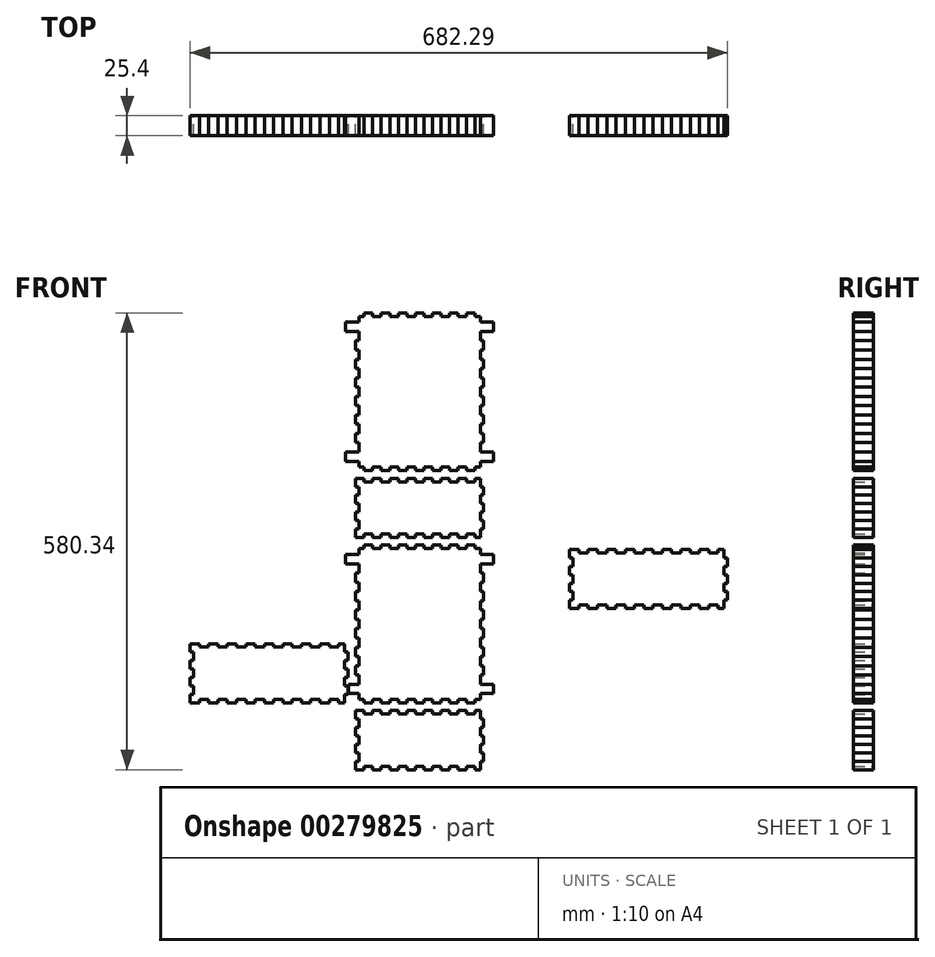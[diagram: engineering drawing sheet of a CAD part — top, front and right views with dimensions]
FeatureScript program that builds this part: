
annotation { "Feature Type Name" : "Feature", "Feature Type Description" : "" }
export const myFeature = defineFeature(function(context is Context, id is Id, definition is map)
    precondition{}
    {
        {
            var Q0;
            Q0=qCreatedBy(makeId("Front.planeOp"),FACE);
            var sketch = newSketch(context, id + "F0", { "sketchPlane" : qUnion([Q0])});
            skLineSegment(sketch, "E0", {"start": v(-81.37, -290.17) * mm, "end": v(-70.52, -290.17) * mm});
            skLineSegment(sketch, "E1", {"start": v(-70.52, -285.8) * mm, "end": v(-70.52, -290.17) * mm});
            skLineSegment(sketch, "E2", {"start": v(-70.52, -285.8) * mm, "end": v(-59.67, -285.8) * mm});
            skLineSegment(sketch, "E3", {"start": v(-59.67, -285.8) * mm, "end": v(-59.67, -290.17) * mm});
            skLineSegment(sketch, "E4", {"start": v(-59.67, -290.17) * mm, "end": v(-48.82, -290.17) * mm});
            skLineSegment(sketch, "E5", {"start": v(-48.82, -285.8) * mm, "end": v(-48.82, -290.17) * mm});
            skLineSegment(sketch, "E6", {"start": v(-48.82, -285.8) * mm, "end": v(-37.97, -285.8) * mm});
            skLineSegment(sketch, "E7", {"start": v(-37.97, -285.8) * mm, "end": v(-37.97, -290.17) * mm});
            skLineSegment(sketch, "E8", {"start": v(-37.97, -290.17) * mm, "end": v(-27.12, -290.17) * mm});
            skLineSegment(sketch, "E9", {"start": v(-27.12, -285.8) * mm, "end": v(-27.12, -290.17) * mm});
            skLineSegment(sketch, "E10", {"start": v(-27.12, -285.8) * mm, "end": v(-16.27, -285.8) * mm});
            skLineSegment(sketch, "E11", {"start": v(-16.27, -285.8) * mm, "end": v(-16.27, -290.17) * mm});
            skLineSegment(sketch, "E12", {"start": v(-16.27, -290.17) * mm, "end": v(-5.42, -290.17) * mm});
            skLineSegment(sketch, "E13", {"start": v(-5.42, -285.8) * mm, "end": v(-5.42, -290.17) * mm});
            skLineSegment(sketch, "E14", {"start": v(-5.42, -285.8) * mm, "end": v(5.42, -285.8) * mm});
            skLineSegment(sketch, "E15", {"start": v(5.42, -285.8) * mm, "end": v(5.42, -290.17) * mm});
            skLineSegment(sketch, "E16", {"start": v(5.42, -290.17) * mm, "end": v(16.27, -290.17) * mm});
            skLineSegment(sketch, "E17", {"start": v(16.27, -285.8) * mm, "end": v(16.27, -290.17) * mm});
            skLineSegment(sketch, "E18", {"start": v(16.27, -285.8) * mm, "end": v(27.12, -285.8) * mm});
            skLineSegment(sketch, "E19", {"start": v(27.12, -285.8) * mm, "end": v(27.12, -290.17) * mm});
            skLineSegment(sketch, "E20", {"start": v(27.12, -290.17) * mm, "end": v(37.97, -290.17) * mm});
            skLineSegment(sketch, "E21", {"start": v(37.97, -285.8) * mm, "end": v(37.97, -290.17) * mm});
            skLineSegment(sketch, "E22", {"start": v(37.97, -285.8) * mm, "end": v(48.82, -285.8) * mm});
            skLineSegment(sketch, "E23", {"start": v(48.82, -285.8) * mm, "end": v(48.82, -290.17) * mm});
            skLineSegment(sketch, "E24", {"start": v(48.82, -290.17) * mm, "end": v(59.67, -290.17) * mm});
            skLineSegment(sketch, "E25", {"start": v(59.67, -285.8) * mm, "end": v(59.67, -290.17) * mm});
            skLineSegment(sketch, "E26", {"start": v(59.67, -285.8) * mm, "end": v(70.51, -285.8) * mm});
            skLineSegment(sketch, "E27", {"start": v(70.51, -285.8) * mm, "end": v(70.51, -290.17) * mm});
            skLineSegment(sketch, "E28", {"start": v(70.51, -290.17) * mm, "end": v(76.98, -290.17) * mm});
            skLineSegment(sketch, "E29", {"start": v(-81.37, -215.07) * mm, "end": v(-70.52, -215.07) * mm});
            skLineSegment(sketch, "E30", {"start": v(-70.52, -215.07) * mm, "end": v(-70.52, -219.45) * mm});
            skLineSegment(sketch, "E31", {"start": v(-70.52, -219.45) * mm, "end": v(-59.67, -219.45) * mm});
            skLineSegment(sketch, "E32", {"start": v(-59.67, -215.07) * mm, "end": v(-59.67, -219.45) * mm});
            skLineSegment(sketch, "E33", {"start": v(-59.67, -215.07) * mm, "end": v(-48.82, -215.07) * mm});
            skLineSegment(sketch, "E34", {"start": v(-48.82, -215.07) * mm, "end": v(-48.82, -219.45) * mm});
            skLineSegment(sketch, "E35", {"start": v(-48.82, -219.45) * mm, "end": v(-37.97, -219.45) * mm});
            skLineSegment(sketch, "E36", {"start": v(-37.97, -215.07) * mm, "end": v(-37.97, -219.45) * mm});
            skLineSegment(sketch, "E37", {"start": v(-37.97, -215.07) * mm, "end": v(-27.12, -215.07) * mm});
            skLineSegment(sketch, "E38", {"start": v(-27.12, -215.07) * mm, "end": v(-27.12, -219.45) * mm});
            skLineSegment(sketch, "E39", {"start": v(-27.12, -219.45) * mm, "end": v(-16.27, -219.45) * mm});
            skLineSegment(sketch, "E40", {"start": v(-16.27, -215.07) * mm, "end": v(-16.27, -219.45) * mm});
            skLineSegment(sketch, "E41", {"start": v(-16.27, -215.07) * mm, "end": v(-5.42, -215.07) * mm});
            skLineSegment(sketch, "E42", {"start": v(-5.42, -215.07) * mm, "end": v(-5.42, -219.45) * mm});
            skLineSegment(sketch, "E43", {"start": v(-5.42, -219.45) * mm, "end": v(5.42, -219.45) * mm});
            skLineSegment(sketch, "E44", {"start": v(5.42, -215.07) * mm, "end": v(5.42, -219.45) * mm});
            skLineSegment(sketch, "E45", {"start": v(5.42, -215.07) * mm, "end": v(16.27, -215.07) * mm});
            skLineSegment(sketch, "E46", {"start": v(16.27, -215.07) * mm, "end": v(16.27, -219.45) * mm});
            skLineSegment(sketch, "E47", {"start": v(16.27, -219.45) * mm, "end": v(27.12, -219.45) * mm});
            skLineSegment(sketch, "E48", {"start": v(27.12, -215.07) * mm, "end": v(27.12, -219.45) * mm});
            skLineSegment(sketch, "E49", {"start": v(27.12, -215.07) * mm, "end": v(37.97, -215.07) * mm});
            skLineSegment(sketch, "E50", {"start": v(37.97, -215.07) * mm, "end": v(37.97, -219.45) * mm});
            skLineSegment(sketch, "E51", {"start": v(37.97, -219.45) * mm, "end": v(48.82, -219.45) * mm});
            skLineSegment(sketch, "E52", {"start": v(48.82, -215.07) * mm, "end": v(48.82, -219.45) * mm});
            skLineSegment(sketch, "E53", {"start": v(48.82, -215.07) * mm, "end": v(59.67, -215.07) * mm});
            skLineSegment(sketch, "E54", {"start": v(59.67, -215.07) * mm, "end": v(59.67, -219.45) * mm});
            skLineSegment(sketch, "E55", {"start": v(59.67, -219.45) * mm, "end": v(70.51, -219.45) * mm});
            skLineSegment(sketch, "E56", {"start": v(70.51, -215.07) * mm, "end": v(70.51, -219.45) * mm});
            skLineSegment(sketch, "E57", {"start": v(70.51, -215.07) * mm, "end": v(76.98, -215.07) * mm});
            skLineSegment(sketch, "E58", {"start": v(-81.37, -290.17) * mm, "end": v(-81.37, -279.44) * mm});
            skLineSegment(sketch, "E59", {"start": v(-76.98, -279.44) * mm, "end": v(-81.37, -279.44) * mm});
            skLineSegment(sketch, "E60", {"start": v(-76.98, -279.44) * mm, "end": v(-76.98, -268.71) * mm});
            skLineSegment(sketch, "E61", {"start": v(-76.98, -268.71) * mm, "end": v(-81.37, -268.71) * mm});
            skLineSegment(sketch, "E62", {"start": v(-81.37, -268.71) * mm, "end": v(-81.37, -257.99) * mm});
            skLineSegment(sketch, "E63", {"start": v(-76.98, -257.99) * mm, "end": v(-81.37, -257.99) * mm});
            skLineSegment(sketch, "E64", {"start": v(-76.98, -257.99) * mm, "end": v(-76.98, -247.26) * mm});
            skLineSegment(sketch, "E65", {"start": v(-76.98, -247.26) * mm, "end": v(-81.37, -247.26) * mm});
            skLineSegment(sketch, "E66", {"start": v(-81.37, -247.26) * mm, "end": v(-81.37, -236.53) * mm});
            skLineSegment(sketch, "E67", {"start": v(-76.98, -236.53) * mm, "end": v(-81.37, -236.53) * mm});
            skLineSegment(sketch, "E68", {"start": v(-76.98, -236.53) * mm, "end": v(-76.98, -225.8) * mm});
            skLineSegment(sketch, "E69", {"start": v(-76.98, -225.8) * mm, "end": v(-81.37, -225.8) * mm});
            skLineSegment(sketch, "E70", {"start": v(-81.37, -225.8) * mm, "end": v(-81.37, -215.07) * mm});
            skLineSegment(sketch, "E71", {"start": v(76.98, -290.17) * mm, "end": v(76.98, -279.44) * mm});
            skLineSegment(sketch, "E72", {"start": v(81.36, -279.44) * mm, "end": v(76.98, -279.44) * mm});
            skLineSegment(sketch, "E73", {"start": v(81.36, -279.44) * mm, "end": v(81.36, -268.71) * mm});
            skLineSegment(sketch, "E74", {"start": v(81.36, -268.71) * mm, "end": v(76.98, -268.71) * mm});
            skLineSegment(sketch, "E75", {"start": v(76.98, -268.71) * mm, "end": v(76.98, -257.99) * mm});
            skLineSegment(sketch, "E76", {"start": v(81.36, -257.99) * mm, "end": v(76.98, -257.99) * mm});
            skLineSegment(sketch, "E77", {"start": v(81.36, -257.99) * mm, "end": v(81.36, -247.26) * mm});
            skLineSegment(sketch, "E78", {"start": v(81.36, -247.26) * mm, "end": v(76.98, -247.26) * mm});
            skLineSegment(sketch, "E79", {"start": v(76.98, -247.26) * mm, "end": v(76.98, -236.53) * mm});
            skLineSegment(sketch, "E80", {"start": v(81.36, -236.53) * mm, "end": v(76.98, -236.53) * mm});
            skLineSegment(sketch, "E81", {"start": v(81.36, -236.53) * mm, "end": v(81.36, -225.8) * mm});
            skLineSegment(sketch, "E82", {"start": v(81.36, -225.8) * mm, "end": v(76.98, -225.8) * mm});
            skLineSegment(sketch, "E83", {"start": v(76.98, -225.8) * mm, "end": v(76.98, -215.07) * mm});
            skLineSegment(sketch, "E84", {"start": v(-291.5, -205.21) * mm, "end": v(-279.72, -205.21) * mm});
            skLineSegment(sketch, "E85", {"start": v(-279.72, -200.83) * mm, "end": v(-279.72, -205.21) * mm});
            skLineSegment(sketch, "E86", {"start": v(-279.72, -200.83) * mm, "end": v(-267.94, -200.83) * mm});
            skLineSegment(sketch, "E87", {"start": v(-267.94, -200.83) * mm, "end": v(-267.94, -205.21) * mm});
            skLineSegment(sketch, "E88", {"start": v(-267.94, -205.21) * mm, "end": v(-256.16, -205.21) * mm});
            skLineSegment(sketch, "E89", {"start": v(-256.16, -200.83) * mm, "end": v(-256.16, -205.21) * mm});
            skLineSegment(sketch, "E90", {"start": v(-256.16, -200.83) * mm, "end": v(-244.38, -200.83) * mm});
            skLineSegment(sketch, "E91", {"start": v(-244.38, -200.83) * mm, "end": v(-244.38, -205.21) * mm});
            skLineSegment(sketch, "E92", {"start": v(-244.38, -205.21) * mm, "end": v(-232.6, -205.21) * mm});
            skLineSegment(sketch, "E93", {"start": v(-232.6, -200.83) * mm, "end": v(-232.6, -205.21) * mm});
            skLineSegment(sketch, "E94", {"start": v(-232.6, -200.83) * mm, "end": v(-220.81, -200.83) * mm});
            skLineSegment(sketch, "E95", {"start": v(-220.81, -200.83) * mm, "end": v(-220.81, -205.21) * mm});
            skLineSegment(sketch, "E96", {"start": v(-220.81, -205.21) * mm, "end": v(-209.03, -205.21) * mm});
            skLineSegment(sketch, "E97", {"start": v(-209.03, -200.83) * mm, "end": v(-209.03, -205.21) * mm});
            skLineSegment(sketch, "E98", {"start": v(-209.03, -200.83) * mm, "end": v(-197.25, -200.83) * mm});
            skLineSegment(sketch, "E99", {"start": v(-197.25, -200.83) * mm, "end": v(-197.25, -205.21) * mm});
            skLineSegment(sketch, "E100", {"start": v(-197.25, -205.21) * mm, "end": v(-185.47, -205.21) * mm});
            skLineSegment(sketch, "E101", {"start": v(-185.47, -200.83) * mm, "end": v(-185.47, -205.21) * mm});
            skLineSegment(sketch, "E102", {"start": v(-185.47, -200.83) * mm, "end": v(-173.69, -200.83) * mm});
            skLineSegment(sketch, "E103", {"start": v(-173.69, -200.83) * mm, "end": v(-173.69, -205.21) * mm});
            skLineSegment(sketch, "E104", {"start": v(-173.69, -205.21) * mm, "end": v(-161.9, -205.21) * mm});
            skLineSegment(sketch, "E105", {"start": v(-161.9, -200.83) * mm, "end": v(-161.9, -205.21) * mm});
            skLineSegment(sketch, "E106", {"start": v(-161.9, -200.83) * mm, "end": v(-150.13, -200.83) * mm});
            skLineSegment(sketch, "E107", {"start": v(-150.13, -200.83) * mm, "end": v(-150.13, -205.21) * mm});
            skLineSegment(sketch, "E108", {"start": v(-150.13, -205.21) * mm, "end": v(-138.35, -205.21) * mm});
            skLineSegment(sketch, "E109", {"start": v(-138.35, -200.83) * mm, "end": v(-138.35, -205.21) * mm});
            skLineSegment(sketch, "E110", {"start": v(-138.35, -200.83) * mm, "end": v(-126.56, -200.83) * mm});
            skLineSegment(sketch, "E111", {"start": v(-126.56, -200.83) * mm, "end": v(-126.56, -205.21) * mm});
            skLineSegment(sketch, "E112", {"start": v(-126.56, -205.21) * mm, "end": v(-114.78, -205.21) * mm});
            skLineSegment(sketch, "E113", {"start": v(-114.78, -200.83) * mm, "end": v(-114.78, -205.21) * mm});
            skLineSegment(sketch, "E114", {"start": v(-114.78, -200.83) * mm, "end": v(-103, -200.83) * mm});
            skLineSegment(sketch, "E115", {"start": v(-103, -200.83) * mm, "end": v(-103, -205.21) * mm});
            skLineSegment(sketch, "E116", {"start": v(-103, -205.21) * mm, "end": v(-95.6, -205.21) * mm});
            skLineSegment(sketch, "E117", {"start": v(-291.5, -130.1) * mm, "end": v(-279.72, -130.1) * mm});
            skLineSegment(sketch, "E118", {"start": v(-279.72, -130.1) * mm, "end": v(-279.72, -134.49) * mm});
            skLineSegment(sketch, "E119", {"start": v(-279.72, -134.49) * mm, "end": v(-267.94, -134.49) * mm});
            skLineSegment(sketch, "E120", {"start": v(-267.94, -130.1) * mm, "end": v(-267.94, -134.49) * mm});
            skLineSegment(sketch, "E121", {"start": v(-267.94, -130.1) * mm, "end": v(-256.16, -130.1) * mm});
            skLineSegment(sketch, "E122", {"start": v(-256.16, -130.1) * mm, "end": v(-256.16, -134.49) * mm});
            skLineSegment(sketch, "E123", {"start": v(-256.16, -134.49) * mm, "end": v(-244.38, -134.49) * mm});
            skLineSegment(sketch, "E124", {"start": v(-244.38, -130.1) * mm, "end": v(-244.38, -134.49) * mm});
            skLineSegment(sketch, "E125", {"start": v(-244.38, -130.1) * mm, "end": v(-232.6, -130.1) * mm});
            skLineSegment(sketch, "E126", {"start": v(-232.6, -130.1) * mm, "end": v(-232.6, -134.49) * mm});
            skLineSegment(sketch, "E127", {"start": v(-232.6, -134.49) * mm, "end": v(-220.81, -134.49) * mm});
            skLineSegment(sketch, "E128", {"start": v(-220.81, -130.1) * mm, "end": v(-220.81, -134.49) * mm});
            skLineSegment(sketch, "E129", {"start": v(-220.81, -130.1) * mm, "end": v(-209.03, -130.1) * mm});
            skLineSegment(sketch, "E130", {"start": v(-209.03, -130.1) * mm, "end": v(-209.03, -134.49) * mm});
            skLineSegment(sketch, "E131", {"start": v(-209.03, -134.49) * mm, "end": v(-197.25, -134.49) * mm});
            skLineSegment(sketch, "E132", {"start": v(-197.25, -130.1) * mm, "end": v(-197.25, -134.49) * mm});
            skLineSegment(sketch, "E133", {"start": v(-197.25, -130.1) * mm, "end": v(-185.47, -130.1) * mm});
            skLineSegment(sketch, "E134", {"start": v(-185.47, -130.1) * mm, "end": v(-185.47, -134.49) * mm});
            skLineSegment(sketch, "E135", {"start": v(-185.47, -134.49) * mm, "end": v(-173.69, -134.49) * mm});
            skLineSegment(sketch, "E136", {"start": v(-173.69, -130.1) * mm, "end": v(-173.69, -134.49) * mm});
            skLineSegment(sketch, "E137", {"start": v(-173.69, -130.1) * mm, "end": v(-161.9, -130.1) * mm});
            skLineSegment(sketch, "E138", {"start": v(-161.9, -130.1) * mm, "end": v(-161.9, -134.49) * mm});
            skLineSegment(sketch, "E139", {"start": v(-161.9, -134.49) * mm, "end": v(-150.13, -134.49) * mm});
            skLineSegment(sketch, "E140", {"start": v(-150.13, -130.1) * mm, "end": v(-150.13, -134.49) * mm});
            skLineSegment(sketch, "E141", {"start": v(-150.13, -130.1) * mm, "end": v(-138.35, -130.1) * mm});
            skLineSegment(sketch, "E142", {"start": v(-138.35, -130.1) * mm, "end": v(-138.35, -134.49) * mm});
            skLineSegment(sketch, "E143", {"start": v(-138.35, -134.49) * mm, "end": v(-126.56, -134.49) * mm});
            skLineSegment(sketch, "E144", {"start": v(-126.56, -130.1) * mm, "end": v(-126.56, -134.49) * mm});
            skLineSegment(sketch, "E145", {"start": v(-126.56, -130.1) * mm, "end": v(-114.78, -130.1) * mm});
            skLineSegment(sketch, "E146", {"start": v(-114.78, -130.1) * mm, "end": v(-114.78, -134.49) * mm});
            skLineSegment(sketch, "E147", {"start": v(-114.78, -134.49) * mm, "end": v(-103, -134.49) * mm});
            skLineSegment(sketch, "E148", {"start": v(-103, -130.1) * mm, "end": v(-103, -134.49) * mm});
            skLineSegment(sketch, "E149", {"start": v(-103, -130.1) * mm, "end": v(-95.6, -130.1) * mm});
            skLineSegment(sketch, "E150", {"start": v(-291.5, -205.21) * mm, "end": v(-291.5, -194.48) * mm});
            skLineSegment(sketch, "E151", {"start": v(-287.12, -194.48) * mm, "end": v(-291.5, -194.48) * mm});
            skLineSegment(sketch, "E152", {"start": v(-287.12, -194.48) * mm, "end": v(-287.12, -183.75) * mm});
            skLineSegment(sketch, "E153", {"start": v(-287.12, -183.75) * mm, "end": v(-291.5, -183.75) * mm});
            skLineSegment(sketch, "E154", {"start": v(-291.5, -183.75) * mm, "end": v(-291.5, -173.02) * mm});
            skLineSegment(sketch, "E155", {"start": v(-287.12, -173.02) * mm, "end": v(-291.5, -173.02) * mm});
            skLineSegment(sketch, "E156", {"start": v(-287.12, -173.02) * mm, "end": v(-287.12, -162.3) * mm});
            skLineSegment(sketch, "E157", {"start": v(-287.12, -162.3) * mm, "end": v(-291.5, -162.3) * mm});
            skLineSegment(sketch, "E158", {"start": v(-291.5, -162.3) * mm, "end": v(-291.5, -151.56) * mm});
            skLineSegment(sketch, "E159", {"start": v(-287.12, -151.56) * mm, "end": v(-291.5, -151.56) * mm});
            skLineSegment(sketch, "E160", {"start": v(-287.12, -151.56) * mm, "end": v(-287.12, -140.84) * mm});
            skLineSegment(sketch, "E161", {"start": v(-287.12, -140.84) * mm, "end": v(-291.5, -140.84) * mm});
            skLineSegment(sketch, "E162", {"start": v(-291.5, -140.84) * mm, "end": v(-291.5, -130.1) * mm});
            skLineSegment(sketch, "E163", {"start": v(-95.6, -205.21) * mm, "end": v(-95.6, -194.48) * mm});
            skLineSegment(sketch, "E164", {"start": v(-91.22, -194.48) * mm, "end": v(-95.6, -194.48) * mm});
            skLineSegment(sketch, "E165", {"start": v(-91.22, -194.48) * mm, "end": v(-91.22, -183.75) * mm});
            skLineSegment(sketch, "E166", {"start": v(-91.22, -183.75) * mm, "end": v(-95.6, -183.75) * mm});
            skLineSegment(sketch, "E167", {"start": v(-95.6, -183.75) * mm, "end": v(-95.6, -173.02) * mm});
            skLineSegment(sketch, "E168", {"start": v(-91.22, -173.02) * mm, "end": v(-95.6, -173.02) * mm});
            skLineSegment(sketch, "E169", {"start": v(-91.22, -173.02) * mm, "end": v(-91.22, -162.3) * mm});
            skLineSegment(sketch, "E170", {"start": v(-91.22, -162.3) * mm, "end": v(-95.6, -162.3) * mm});
            skLineSegment(sketch, "E171", {"start": v(-95.6, -162.3) * mm, "end": v(-95.6, -151.56) * mm});
            skLineSegment(sketch, "E172", {"start": v(-91.22, -151.56) * mm, "end": v(-95.6, -151.56) * mm});
            skLineSegment(sketch, "E173", {"start": v(-91.22, -151.56) * mm, "end": v(-91.22, -140.84) * mm});
            skLineSegment(sketch, "E174", {"start": v(-91.22, -140.84) * mm, "end": v(-95.6, -140.84) * mm});
            skLineSegment(sketch, "E175", {"start": v(-95.6, -140.84) * mm, "end": v(-95.6, -130.1) * mm});
            skLineSegment(sketch, "E176", {"start": v(-76.98, -200.83) * mm, "end": v(-70.52, -200.83) * mm});
            skLineSegment(sketch, "E177", {"start": v(-70.52, -200.83) * mm, "end": v(-70.52, -205.21) * mm});
            skLineSegment(sketch, "E178", {"start": v(-70.52, -205.21) * mm, "end": v(-59.67, -205.21) * mm});
            skLineSegment(sketch, "E179", {"start": v(-59.67, -200.83) * mm, "end": v(-59.67, -205.21) * mm});
            skLineSegment(sketch, "E180", {"start": v(-59.67, -200.83) * mm, "end": v(-48.82, -200.83) * mm});
            skLineSegment(sketch, "E181", {"start": v(-48.82, -200.83) * mm, "end": v(-48.82, -205.21) * mm});
            skLineSegment(sketch, "E182", {"start": v(-48.82, -205.21) * mm, "end": v(-37.97, -205.21) * mm});
            skLineSegment(sketch, "E183", {"start": v(-37.97, -200.83) * mm, "end": v(-37.97, -205.21) * mm});
            skLineSegment(sketch, "E184", {"start": v(-37.97, -200.83) * mm, "end": v(-27.12, -200.83) * mm});
            skLineSegment(sketch, "E185", {"start": v(-27.12, -200.83) * mm, "end": v(-27.12, -205.21) * mm});
            skLineSegment(sketch, "E186", {"start": v(-27.12, -205.21) * mm, "end": v(-16.27, -205.21) * mm});
            skLineSegment(sketch, "E187", {"start": v(-16.27, -200.83) * mm, "end": v(-16.27, -205.21) * mm});
            skLineSegment(sketch, "E188", {"start": v(-16.27, -200.83) * mm, "end": v(-5.42, -200.83) * mm});
            skLineSegment(sketch, "E189", {"start": v(-5.42, -200.83) * mm, "end": v(-5.42, -205.21) * mm});
            skLineSegment(sketch, "E190", {"start": v(-5.42, -205.21) * mm, "end": v(5.42, -205.21) * mm});
            skLineSegment(sketch, "E191", {"start": v(5.42, -200.83) * mm, "end": v(5.42, -205.21) * mm});
            skLineSegment(sketch, "E192", {"start": v(5.42, -200.83) * mm, "end": v(16.27, -200.83) * mm});
            skLineSegment(sketch, "E193", {"start": v(16.27, -200.83) * mm, "end": v(16.27, -205.21) * mm});
            skLineSegment(sketch, "E194", {"start": v(16.27, -205.21) * mm, "end": v(27.12, -205.21) * mm});
            skLineSegment(sketch, "E195", {"start": v(27.12, -200.83) * mm, "end": v(27.12, -205.21) * mm});
            skLineSegment(sketch, "E196", {"start": v(27.12, -200.83) * mm, "end": v(37.97, -200.83) * mm});
            skLineSegment(sketch, "E197", {"start": v(37.97, -200.83) * mm, "end": v(37.97, -205.21) * mm});
            skLineSegment(sketch, "E198", {"start": v(37.97, -205.21) * mm, "end": v(48.82, -205.21) * mm});
            skLineSegment(sketch, "E199", {"start": v(48.82, -200.83) * mm, "end": v(48.82, -205.21) * mm});
            skLineSegment(sketch, "E200", {"start": v(48.82, -200.83) * mm, "end": v(59.67, -200.83) * mm});
            skLineSegment(sketch, "E201", {"start": v(59.67, -200.83) * mm, "end": v(59.67, -205.21) * mm});
            skLineSegment(sketch, "E202", {"start": v(59.67, -205.21) * mm, "end": v(70.51, -205.21) * mm});
            skLineSegment(sketch, "E203", {"start": v(70.51, -200.83) * mm, "end": v(70.51, -205.21) * mm});
            skLineSegment(sketch, "E204", {"start": v(70.51, -200.83) * mm, "end": v(76.98, -200.83) * mm});
            skLineSegment(sketch, "E205", {"start": v(-76.98, -9.31) * mm, "end": v(-70.52, -9.31) * mm});
            skLineSegment(sketch, "E206", {"start": v(-70.52, -4.93) * mm, "end": v(-70.52, -9.31) * mm});
            skLineSegment(sketch, "E207", {"start": v(-70.52, -4.93) * mm, "end": v(-59.67, -4.93) * mm});
            skLineSegment(sketch, "E208", {"start": v(-59.67, -4.93) * mm, "end": v(-59.67, -9.31) * mm});
            skLineSegment(sketch, "E209", {"start": v(-59.67, -9.31) * mm, "end": v(-48.82, -9.31) * mm});
            skLineSegment(sketch, "E210", {"start": v(-48.82, -4.93) * mm, "end": v(-48.82, -9.31) * mm});
            skLineSegment(sketch, "E211", {"start": v(-48.82, -4.93) * mm, "end": v(-37.97, -4.93) * mm});
            skLineSegment(sketch, "E212", {"start": v(-37.97, -4.93) * mm, "end": v(-37.97, -9.31) * mm});
            skLineSegment(sketch, "E213", {"start": v(-37.97, -9.31) * mm, "end": v(-27.12, -9.31) * mm});
            skLineSegment(sketch, "E214", {"start": v(-27.12, -4.93) * mm, "end": v(-27.12, -9.31) * mm});
            skLineSegment(sketch, "E215", {"start": v(-27.12, -4.93) * mm, "end": v(-16.27, -4.93) * mm});
            skLineSegment(sketch, "E216", {"start": v(-16.27, -4.93) * mm, "end": v(-16.27, -9.31) * mm});
            skLineSegment(sketch, "E217", {"start": v(-16.27, -9.31) * mm, "end": v(-5.42, -9.31) * mm});
            skLineSegment(sketch, "E218", {"start": v(-5.42, -4.93) * mm, "end": v(-5.42, -9.31) * mm});
            skLineSegment(sketch, "E219", {"start": v(-5.42, -4.93) * mm, "end": v(5.42, -4.93) * mm});
            skLineSegment(sketch, "E220", {"start": v(5.42, -4.93) * mm, "end": v(5.42, -9.31) * mm});
            skLineSegment(sketch, "E221", {"start": v(5.42, -9.31) * mm, "end": v(16.27, -9.31) * mm});
            skLineSegment(sketch, "E222", {"start": v(16.27, -4.93) * mm, "end": v(16.27, -9.31) * mm});
            skLineSegment(sketch, "E223", {"start": v(16.27, -4.93) * mm, "end": v(27.12, -4.93) * mm});
            skLineSegment(sketch, "E224", {"start": v(27.12, -4.93) * mm, "end": v(27.12, -9.31) * mm});
            skLineSegment(sketch, "E225", {"start": v(27.12, -9.31) * mm, "end": v(37.97, -9.31) * mm});
            skLineSegment(sketch, "E226", {"start": v(37.97, -4.93) * mm, "end": v(37.97, -9.31) * mm});
            skLineSegment(sketch, "E227", {"start": v(37.97, -4.93) * mm, "end": v(48.82, -4.93) * mm});
            skLineSegment(sketch, "E228", {"start": v(48.82, -4.93) * mm, "end": v(48.82, -9.31) * mm});
            skLineSegment(sketch, "E229", {"start": v(48.82, -9.31) * mm, "end": v(59.67, -9.31) * mm});
            skLineSegment(sketch, "E230", {"start": v(59.67, -4.93) * mm, "end": v(59.67, -9.31) * mm});
            skLineSegment(sketch, "E231", {"start": v(59.67, -4.93) * mm, "end": v(70.51, -4.93) * mm});
            skLineSegment(sketch, "E232", {"start": v(70.51, -4.93) * mm, "end": v(70.51, -9.31) * mm});
            skLineSegment(sketch, "E233", {"start": v(70.51, -9.31) * mm, "end": v(76.98, -9.31) * mm});
            skLineSegment(sketch, "E234", {"start": v(-76.98, -200.83) * mm, "end": v(-76.98, -193.43) * mm});
            skLineSegment(sketch, "E235", {"start": v(-73.26, -193.43) * mm, "end": v(-77.64, -193.43) * mm});
            skLineSegment(sketch, "E236", {"start": v(-76.98, -181.65) * mm, "end": v(-81.37, -181.65) * mm});
            skLineSegment(sketch, "E237", {"start": v(-76.98, -181.65) * mm, "end": v(-76.98, -169.87) * mm});
            skLineSegment(sketch, "E238", {"start": v(-76.98, -169.87) * mm, "end": v(-81.37, -169.87) * mm});
            skLineSegment(sketch, "E239", {"start": v(-81.37, -169.87) * mm, "end": v(-81.37, -158.09) * mm});
            skLineSegment(sketch, "E240", {"start": v(-76.98, -158.09) * mm, "end": v(-81.37, -158.09) * mm});
            skLineSegment(sketch, "E241", {"start": v(-76.98, -158.09) * mm, "end": v(-76.98, -146.3) * mm});
            skLineSegment(sketch, "E242", {"start": v(-76.98, -146.3) * mm, "end": v(-81.37, -146.3) * mm});
            skLineSegment(sketch, "E243", {"start": v(-81.37, -146.3) * mm, "end": v(-81.37, -134.52) * mm});
            skLineSegment(sketch, "E244", {"start": v(-76.98, -134.52) * mm, "end": v(-81.37, -134.52) * mm});
            skLineSegment(sketch, "E245", {"start": v(-76.98, -134.52) * mm, "end": v(-76.98, -122.74) * mm});
            skLineSegment(sketch, "E246", {"start": v(-76.98, -122.74) * mm, "end": v(-81.37, -122.74) * mm});
            skLineSegment(sketch, "E247", {"start": v(-81.37, -122.74) * mm, "end": v(-81.37, -110.96) * mm});
            skLineSegment(sketch, "E248", {"start": v(-76.98, -110.96) * mm, "end": v(-81.37, -110.96) * mm});
            skLineSegment(sketch, "E249", {"start": v(-76.98, -110.96) * mm, "end": v(-76.98, -99.18) * mm});
            skLineSegment(sketch, "E250", {"start": v(-76.98, -99.18) * mm, "end": v(-81.37, -99.18) * mm});
            skLineSegment(sketch, "E251", {"start": v(-81.37, -99.18) * mm, "end": v(-81.37, -87.4) * mm});
            skLineSegment(sketch, "E252", {"start": v(-76.98, -87.4) * mm, "end": v(-81.37, -87.4) * mm});
            skLineSegment(sketch, "E253", {"start": v(-76.98, -87.4) * mm, "end": v(-76.98, -75.62) * mm});
            skLineSegment(sketch, "E254", {"start": v(-76.98, -75.62) * mm, "end": v(-81.37, -75.62) * mm});
            skLineSegment(sketch, "E255", {"start": v(-81.37, -75.62) * mm, "end": v(-81.37, -63.84) * mm});
            skLineSegment(sketch, "E256", {"start": v(-76.98, -63.84) * mm, "end": v(-81.37, -63.84) * mm});
            skLineSegment(sketch, "E257", {"start": v(-76.98, -63.84) * mm, "end": v(-76.98, -52.05) * mm});
            skLineSegment(sketch, "E258", {"start": v(-76.98, -52.05) * mm, "end": v(-81.37, -52.05) * mm});
            skLineSegment(sketch, "E259", {"start": v(-81.37, -52.05) * mm, "end": v(-81.37, -40.27) * mm});
            skLineSegment(sketch, "E260", {"start": v(-76.98, -40.27) * mm, "end": v(-81.37, -40.27) * mm});
            skLineSegment(sketch, "E261", {"start": v(-76.98, -40.27) * mm, "end": v(-76.98, -28.5) * mm});
            skLineSegment(sketch, "E262", {"start": v(-76.98, -28.5) * mm, "end": v(-81.37, -28.5) * mm});
            skLineSegment(sketch, "E263", {"start": v(-76.98, -16.71) * mm, "end": v(-81.37, -16.71) * mm});
            skLineSegment(sketch, "E264", {"start": v(-76.98, -16.71) * mm, "end": v(-76.98, -9.31) * mm});
            skLineSegment(sketch, "E265", {"start": v(76.98, -200.83) * mm, "end": v(76.98, -193.43) * mm});
            skLineSegment(sketch, "E266", {"start": v(85.75, -193.43) * mm, "end": v(81.36, -193.43) * mm});
            skLineSegment(sketch, "E267", {"start": v(81.36, -181.65) * mm, "end": v(76.98, -181.65) * mm});
            skLineSegment(sketch, "E268", {"start": v(76.98, -181.65) * mm, "end": v(76.98, -169.87) * mm});
            skLineSegment(sketch, "E269", {"start": v(81.36, -169.87) * mm, "end": v(76.98, -169.87) * mm});
            skLineSegment(sketch, "E270", {"start": v(81.36, -169.87) * mm, "end": v(81.36, -158.09) * mm});
            skLineSegment(sketch, "E271", {"start": v(81.36, -158.09) * mm, "end": v(76.98, -158.09) * mm});
            skLineSegment(sketch, "E272", {"start": v(76.98, -158.09) * mm, "end": v(76.98, -146.3) * mm});
            skLineSegment(sketch, "E273", {"start": v(81.36, -146.3) * mm, "end": v(76.98, -146.3) * mm});
            skLineSegment(sketch, "E274", {"start": v(81.36, -146.3) * mm, "end": v(81.36, -134.52) * mm});
            skLineSegment(sketch, "E275", {"start": v(81.36, -134.52) * mm, "end": v(76.98, -134.52) * mm});
            skLineSegment(sketch, "E276", {"start": v(76.98, -134.52) * mm, "end": v(76.98, -122.74) * mm});
            skLineSegment(sketch, "E277", {"start": v(81.36, -122.74) * mm, "end": v(76.98, -122.74) * mm});
            skLineSegment(sketch, "E278", {"start": v(81.36, -122.74) * mm, "end": v(81.36, -110.96) * mm});
            skLineSegment(sketch, "E279", {"start": v(81.36, -110.96) * mm, "end": v(76.98, -110.96) * mm});
            skLineSegment(sketch, "E280", {"start": v(76.98, -110.96) * mm, "end": v(76.98, -99.18) * mm});
            skLineSegment(sketch, "E281", {"start": v(81.36, -99.18) * mm, "end": v(76.98, -99.18) * mm});
            skLineSegment(sketch, "E282", {"start": v(81.36, -99.18) * mm, "end": v(81.36, -87.4) * mm});
            skLineSegment(sketch, "E283", {"start": v(81.36, -87.4) * mm, "end": v(76.98, -87.4) * mm});
            skLineSegment(sketch, "E284", {"start": v(76.98, -87.4) * mm, "end": v(76.98, -75.62) * mm});
            skLineSegment(sketch, "E285", {"start": v(81.36, -75.62) * mm, "end": v(76.98, -75.62) * mm});
            skLineSegment(sketch, "E286", {"start": v(81.36, -75.62) * mm, "end": v(81.36, -63.84) * mm});
            skLineSegment(sketch, "E287", {"start": v(81.36, -63.84) * mm, "end": v(76.98, -63.84) * mm});
            skLineSegment(sketch, "E288", {"start": v(76.98, -63.84) * mm, "end": v(76.98, -52.05) * mm});
            skLineSegment(sketch, "E289", {"start": v(81.36, -52.05) * mm, "end": v(76.98, -52.05) * mm});
            skLineSegment(sketch, "E290", {"start": v(81.36, -52.05) * mm, "end": v(81.36, -40.27) * mm});
            skLineSegment(sketch, "E291", {"start": v(81.36, -40.27) * mm, "end": v(76.98, -40.27) * mm});
            skLineSegment(sketch, "E292", {"start": v(76.98, -40.27) * mm, "end": v(76.98, -28.5) * mm});
            skLineSegment(sketch, "E293", {"start": v(81.36, -28.5) * mm, "end": v(76.98, -28.5) * mm});
            skLineSegment(sketch, "E294", {"start": v(81, -16.71) * mm, "end": v(76.62, -16.71) * mm});
            skLineSegment(sketch, "E295", {"start": v(76.98, -16.71) * mm, "end": v(76.98, -9.31) * mm});
            skLineSegment(sketch, "E296", {"start": v(-81.37, 4.93) * mm, "end": v(-70.52, 4.93) * mm});
            skLineSegment(sketch, "E297", {"start": v(-70.52, 9.3) * mm, "end": v(-70.52, 4.93) * mm});
            skLineSegment(sketch, "E298", {"start": v(-70.52, 9.3) * mm, "end": v(-59.67, 9.3) * mm});
            skLineSegment(sketch, "E299", {"start": v(-59.67, 9.3) * mm, "end": v(-59.67, 4.93) * mm});
            skLineSegment(sketch, "E300", {"start": v(-59.67, 4.93) * mm, "end": v(-48.82, 4.93) * mm});
            skLineSegment(sketch, "E301", {"start": v(-48.82, 9.3) * mm, "end": v(-48.82, 4.93) * mm});
            skLineSegment(sketch, "E302", {"start": v(-48.82, 9.3) * mm, "end": v(-37.97, 9.3) * mm});
            skLineSegment(sketch, "E303", {"start": v(-37.97, 9.3) * mm, "end": v(-37.97, 4.93) * mm});
            skLineSegment(sketch, "E304", {"start": v(-37.97, 4.93) * mm, "end": v(-27.12, 4.93) * mm});
            skLineSegment(sketch, "E305", {"start": v(-27.12, 9.3) * mm, "end": v(-27.12, 4.93) * mm});
            skLineSegment(sketch, "E306", {"start": v(-27.12, 9.3) * mm, "end": v(-16.27, 9.3) * mm});
            skLineSegment(sketch, "E307", {"start": v(-16.27, 9.3) * mm, "end": v(-16.27, 4.93) * mm});
            skLineSegment(sketch, "E308", {"start": v(-16.27, 4.93) * mm, "end": v(-5.42, 4.93) * mm});
            skLineSegment(sketch, "E309", {"start": v(-5.42, 9.3) * mm, "end": v(-5.42, 4.93) * mm});
            skLineSegment(sketch, "E310", {"start": v(-5.42, 9.3) * mm, "end": v(5.42, 9.3) * mm});
            skLineSegment(sketch, "E311", {"start": v(5.42, 9.3) * mm, "end": v(5.42, 4.93) * mm});
            skLineSegment(sketch, "E312", {"start": v(5.42, 4.93) * mm, "end": v(16.27, 4.93) * mm});
            skLineSegment(sketch, "E313", {"start": v(16.27, 9.3) * mm, "end": v(16.27, 4.93) * mm});
            skLineSegment(sketch, "E314", {"start": v(16.27, 9.3) * mm, "end": v(27.12, 9.3) * mm});
            skLineSegment(sketch, "E315", {"start": v(27.12, 9.3) * mm, "end": v(27.12, 4.93) * mm});
            skLineSegment(sketch, "E316", {"start": v(27.12, 4.93) * mm, "end": v(37.97, 4.93) * mm});
            skLineSegment(sketch, "E317", {"start": v(37.97, 9.3) * mm, "end": v(37.97, 4.93) * mm});
            skLineSegment(sketch, "E318", {"start": v(37.97, 9.3) * mm, "end": v(48.82, 9.3) * mm});
            skLineSegment(sketch, "E319", {"start": v(48.82, 9.3) * mm, "end": v(48.82, 4.93) * mm});
            skLineSegment(sketch, "E320", {"start": v(48.82, 4.93) * mm, "end": v(59.67, 4.93) * mm});
            skLineSegment(sketch, "E321", {"start": v(59.67, 9.3) * mm, "end": v(59.67, 4.93) * mm});
            skLineSegment(sketch, "E322", {"start": v(59.67, 9.3) * mm, "end": v(70.51, 9.3) * mm});
            skLineSegment(sketch, "E323", {"start": v(70.51, 9.3) * mm, "end": v(70.51, 4.93) * mm});
            skLineSegment(sketch, "E324", {"start": v(70.51, 4.93) * mm, "end": v(76.98, 4.93) * mm});
            skLineSegment(sketch, "E325", {"start": v(-81.37, 80.03) * mm, "end": v(-70.52, 80.03) * mm});
            skLineSegment(sketch, "E326", {"start": v(-70.52, 80.03) * mm, "end": v(-70.52, 75.65) * mm});
            skLineSegment(sketch, "E327", {"start": v(-70.52, 75.65) * mm, "end": v(-59.67, 75.65) * mm});
            skLineSegment(sketch, "E328", {"start": v(-59.67, 80.03) * mm, "end": v(-59.67, 75.65) * mm});
            skLineSegment(sketch, "E329", {"start": v(-59.67, 80.03) * mm, "end": v(-48.82, 80.03) * mm});
            skLineSegment(sketch, "E330", {"start": v(-48.82, 80.03) * mm, "end": v(-48.82, 75.65) * mm});
            skLineSegment(sketch, "E331", {"start": v(-48.82, 75.65) * mm, "end": v(-37.97, 75.65) * mm});
            skLineSegment(sketch, "E332", {"start": v(-37.97, 80.03) * mm, "end": v(-37.97, 75.65) * mm});
            skLineSegment(sketch, "E333", {"start": v(-37.97, 80.03) * mm, "end": v(-27.12, 80.03) * mm});
            skLineSegment(sketch, "E334", {"start": v(-27.12, 80.03) * mm, "end": v(-27.12, 75.65) * mm});
            skLineSegment(sketch, "E335", {"start": v(-27.12, 75.65) * mm, "end": v(-16.27, 75.65) * mm});
            skLineSegment(sketch, "E336", {"start": v(-16.27, 80.03) * mm, "end": v(-16.27, 75.65) * mm});
            skLineSegment(sketch, "E337", {"start": v(-16.27, 80.03) * mm, "end": v(-5.42, 80.03) * mm});
            skLineSegment(sketch, "E338", {"start": v(-5.42, 80.03) * mm, "end": v(-5.42, 75.65) * mm});
            skLineSegment(sketch, "E339", {"start": v(-5.42, 75.65) * mm, "end": v(5.42, 75.65) * mm});
            skLineSegment(sketch, "E340", {"start": v(5.42, 80.03) * mm, "end": v(5.42, 75.65) * mm});
            skLineSegment(sketch, "E341", {"start": v(5.42, 80.03) * mm, "end": v(16.27, 80.03) * mm});
            skLineSegment(sketch, "E342", {"start": v(16.27, 80.03) * mm, "end": v(16.27, 75.65) * mm});
            skLineSegment(sketch, "E343", {"start": v(16.27, 75.65) * mm, "end": v(27.12, 75.65) * mm});
            skLineSegment(sketch, "E344", {"start": v(27.12, 80.03) * mm, "end": v(27.12, 75.65) * mm});
            skLineSegment(sketch, "E345", {"start": v(27.12, 80.03) * mm, "end": v(37.97, 80.03) * mm});
            skLineSegment(sketch, "E346", {"start": v(37.97, 80.03) * mm, "end": v(37.97, 75.65) * mm});
            skLineSegment(sketch, "E347", {"start": v(37.97, 75.65) * mm, "end": v(48.82, 75.65) * mm});
            skLineSegment(sketch, "E348", {"start": v(48.82, 80.03) * mm, "end": v(48.82, 75.65) * mm});
            skLineSegment(sketch, "E349", {"start": v(48.82, 80.03) * mm, "end": v(59.67, 80.03) * mm});
            skLineSegment(sketch, "E350", {"start": v(59.67, 80.03) * mm, "end": v(59.67, 75.65) * mm});
            skLineSegment(sketch, "E351", {"start": v(59.67, 75.65) * mm, "end": v(70.51, 75.65) * mm});
            skLineSegment(sketch, "E352", {"start": v(70.51, 80.03) * mm, "end": v(70.51, 75.65) * mm});
            skLineSegment(sketch, "E353", {"start": v(70.51, 80.03) * mm, "end": v(76.98, 80.03) * mm});
            skLineSegment(sketch, "E354", {"start": v(-81.37, 4.93) * mm, "end": v(-81.37, 15.66) * mm});
            skLineSegment(sketch, "E355", {"start": v(-76.98, 15.66) * mm, "end": v(-81.37, 15.66) * mm});
            skLineSegment(sketch, "E356", {"start": v(-76.98, 15.66) * mm, "end": v(-76.98, 26.39) * mm});
            skLineSegment(sketch, "E357", {"start": v(-76.98, 26.39) * mm, "end": v(-81.37, 26.39) * mm});
            skLineSegment(sketch, "E358", {"start": v(-81.37, 26.39) * mm, "end": v(-81.37, 37.11) * mm});
            skLineSegment(sketch, "E359", {"start": v(-76.98, 37.11) * mm, "end": v(-81.37, 37.11) * mm});
            skLineSegment(sketch, "E360", {"start": v(-76.98, 37.11) * mm, "end": v(-76.98, 47.84) * mm});
            skLineSegment(sketch, "E361", {"start": v(-76.98, 47.84) * mm, "end": v(-81.37, 47.84) * mm});
            skLineSegment(sketch, "E362", {"start": v(-81.37, 47.84) * mm, "end": v(-81.37, 58.57) * mm});
            skLineSegment(sketch, "E363", {"start": v(-76.98, 58.57) * mm, "end": v(-81.37, 58.57) * mm});
            skLineSegment(sketch, "E364", {"start": v(-76.98, 58.57) * mm, "end": v(-76.98, 69.3) * mm});
            skLineSegment(sketch, "E365", {"start": v(-76.98, 69.3) * mm, "end": v(-81.37, 69.3) * mm});
            skLineSegment(sketch, "E366", {"start": v(-81.37, 69.3) * mm, "end": v(-81.37, 80.03) * mm});
            skLineSegment(sketch, "E367", {"start": v(76.98, 4.93) * mm, "end": v(76.98, 15.66) * mm});
            skLineSegment(sketch, "E368", {"start": v(81.36, 15.66) * mm, "end": v(76.98, 15.66) * mm});
            skLineSegment(sketch, "E369", {"start": v(81.36, 15.66) * mm, "end": v(81.36, 26.39) * mm});
            skLineSegment(sketch, "E370", {"start": v(81.36, 26.39) * mm, "end": v(76.98, 26.39) * mm});
            skLineSegment(sketch, "E371", {"start": v(76.98, 26.39) * mm, "end": v(76.98, 37.11) * mm});
            skLineSegment(sketch, "E372", {"start": v(81.36, 37.11) * mm, "end": v(76.98, 37.11) * mm});
            skLineSegment(sketch, "E373", {"start": v(81.36, 37.11) * mm, "end": v(81.36, 47.84) * mm});
            skLineSegment(sketch, "E374", {"start": v(81.36, 47.84) * mm, "end": v(76.98, 47.84) * mm});
            skLineSegment(sketch, "E375", {"start": v(76.98, 47.84) * mm, "end": v(76.98, 58.57) * mm});
            skLineSegment(sketch, "E376", {"start": v(81.36, 58.57) * mm, "end": v(76.98, 58.57) * mm});
            skLineSegment(sketch, "E377", {"start": v(81.36, 58.57) * mm, "end": v(81.36, 69.3) * mm});
            skLineSegment(sketch, "E378", {"start": v(81.36, 69.3) * mm, "end": v(76.98, 69.3) * mm});
            skLineSegment(sketch, "E379", {"start": v(76.98, 69.3) * mm, "end": v(76.98, 80.03) * mm});
            skLineSegment(sketch, "E380", {"start": v(-76.98, 94.27) * mm, "end": v(-70.52, 94.27) * mm});
            skLineSegment(sketch, "E381", {"start": v(-70.52, 94.27) * mm, "end": v(-70.52, 89.9) * mm});
            skLineSegment(sketch, "E382", {"start": v(-70.52, 89.9) * mm, "end": v(-59.67, 89.9) * mm});
            skLineSegment(sketch, "E383", {"start": v(-59.67, 94.27) * mm, "end": v(-59.67, 89.9) * mm});
            skLineSegment(sketch, "E384", {"start": v(-59.67, 94.27) * mm, "end": v(-48.82, 94.27) * mm});
            skLineSegment(sketch, "E385", {"start": v(-48.82, 94.27) * mm, "end": v(-48.82, 89.9) * mm});
            skLineSegment(sketch, "E386", {"start": v(-48.82, 89.9) * mm, "end": v(-37.97, 89.9) * mm});
            skLineSegment(sketch, "E387", {"start": v(-37.97, 94.27) * mm, "end": v(-37.97, 89.9) * mm});
            skLineSegment(sketch, "E388", {"start": v(-37.97, 94.27) * mm, "end": v(-27.12, 94.27) * mm});
            skLineSegment(sketch, "E389", {"start": v(-27.12, 94.27) * mm, "end": v(-27.12, 89.9) * mm});
            skLineSegment(sketch, "E390", {"start": v(-27.12, 89.9) * mm, "end": v(-16.27, 89.9) * mm});
            skLineSegment(sketch, "E391", {"start": v(-16.27, 94.27) * mm, "end": v(-16.27, 89.9) * mm});
            skLineSegment(sketch, "E392", {"start": v(-16.27, 94.27) * mm, "end": v(-5.42, 94.27) * mm});
            skLineSegment(sketch, "E393", {"start": v(-5.42, 94.27) * mm, "end": v(-5.42, 89.9) * mm});
            skLineSegment(sketch, "E394", {"start": v(-5.42, 89.9) * mm, "end": v(5.42, 89.9) * mm});
            skLineSegment(sketch, "E395", {"start": v(5.42, 94.27) * mm, "end": v(5.42, 89.9) * mm});
            skLineSegment(sketch, "E396", {"start": v(5.42, 94.27) * mm, "end": v(16.27, 94.27) * mm});
            skLineSegment(sketch, "E397", {"start": v(16.27, 94.27) * mm, "end": v(16.27, 89.9) * mm});
            skLineSegment(sketch, "E398", {"start": v(16.27, 89.9) * mm, "end": v(27.12, 89.9) * mm});
            skLineSegment(sketch, "E399", {"start": v(27.12, 94.27) * mm, "end": v(27.12, 89.9) * mm});
            skLineSegment(sketch, "E400", {"start": v(27.12, 94.27) * mm, "end": v(37.97, 94.27) * mm});
            skLineSegment(sketch, "E401", {"start": v(37.97, 94.27) * mm, "end": v(37.97, 89.9) * mm});
            skLineSegment(sketch, "E402", {"start": v(37.97, 89.9) * mm, "end": v(48.82, 89.9) * mm});
            skLineSegment(sketch, "E403", {"start": v(48.82, 94.27) * mm, "end": v(48.82, 89.9) * mm});
            skLineSegment(sketch, "E404", {"start": v(48.82, 94.27) * mm, "end": v(59.67, 94.27) * mm});
            skLineSegment(sketch, "E405", {"start": v(59.67, 94.27) * mm, "end": v(59.67, 89.9) * mm});
            skLineSegment(sketch, "E406", {"start": v(59.67, 89.9) * mm, "end": v(70.51, 89.9) * mm});
            skLineSegment(sketch, "E407", {"start": v(70.51, 94.27) * mm, "end": v(70.51, 89.9) * mm});
            skLineSegment(sketch, "E408", {"start": v(70.51, 94.27) * mm, "end": v(76.98, 94.27) * mm});
            skLineSegment(sketch, "E409", {"start": v(-76.98, 285.8) * mm, "end": v(-70.52, 285.8) * mm});
            skLineSegment(sketch, "E410", {"start": v(-70.52, 290.17) * mm, "end": v(-70.52, 285.8) * mm});
            skLineSegment(sketch, "E411", {"start": v(-70.52, 290.17) * mm, "end": v(-59.67, 290.17) * mm});
            skLineSegment(sketch, "E412", {"start": v(-59.67, 290.17) * mm, "end": v(-59.67, 285.8) * mm});
            skLineSegment(sketch, "E413", {"start": v(-59.67, 285.8) * mm, "end": v(-48.82, 285.8) * mm});
            skLineSegment(sketch, "E414", {"start": v(-48.82, 290.17) * mm, "end": v(-48.82, 285.8) * mm});
            skLineSegment(sketch, "E415", {"start": v(-48.82, 290.17) * mm, "end": v(-37.97, 290.17) * mm});
            skLineSegment(sketch, "E416", {"start": v(-37.97, 290.17) * mm, "end": v(-37.97, 285.8) * mm});
            skLineSegment(sketch, "E417", {"start": v(-37.97, 285.8) * mm, "end": v(-27.12, 285.8) * mm});
            skLineSegment(sketch, "E418", {"start": v(-27.12, 290.17) * mm, "end": v(-27.12, 285.8) * mm});
            skLineSegment(sketch, "E419", {"start": v(-27.12, 290.17) * mm, "end": v(-16.27, 290.17) * mm});
            skLineSegment(sketch, "E420", {"start": v(-16.27, 290.17) * mm, "end": v(-16.27, 285.8) * mm});
            skLineSegment(sketch, "E421", {"start": v(-16.27, 285.8) * mm, "end": v(-5.42, 285.8) * mm});
            skLineSegment(sketch, "E422", {"start": v(-5.42, 290.17) * mm, "end": v(-5.42, 285.8) * mm});
            skLineSegment(sketch, "E423", {"start": v(-5.42, 290.17) * mm, "end": v(5.42, 290.17) * mm});
            skLineSegment(sketch, "E424", {"start": v(5.42, 290.17) * mm, "end": v(5.42, 285.8) * mm});
            skLineSegment(sketch, "E425", {"start": v(5.42, 285.8) * mm, "end": v(16.27, 285.8) * mm});
            skLineSegment(sketch, "E426", {"start": v(16.27, 290.17) * mm, "end": v(16.27, 285.8) * mm});
            skLineSegment(sketch, "E427", {"start": v(16.27, 290.17) * mm, "end": v(27.12, 290.17) * mm});
            skLineSegment(sketch, "E428", {"start": v(27.12, 290.17) * mm, "end": v(27.12, 285.8) * mm});
            skLineSegment(sketch, "E429", {"start": v(27.12, 285.8) * mm, "end": v(37.97, 285.8) * mm});
            skLineSegment(sketch, "E430", {"start": v(37.97, 290.17) * mm, "end": v(37.97, 285.8) * mm});
            skLineSegment(sketch, "E431", {"start": v(37.97, 290.17) * mm, "end": v(48.82, 290.17) * mm});
            skLineSegment(sketch, "E432", {"start": v(48.82, 290.17) * mm, "end": v(48.82, 285.8) * mm});
            skLineSegment(sketch, "E433", {"start": v(48.82, 285.8) * mm, "end": v(59.67, 285.8) * mm});
            skLineSegment(sketch, "E434", {"start": v(59.67, 290.17) * mm, "end": v(59.67, 285.8) * mm});
            skLineSegment(sketch, "E435", {"start": v(59.67, 290.17) * mm, "end": v(70.51, 290.17) * mm});
            skLineSegment(sketch, "E436", {"start": v(70.51, 290.17) * mm, "end": v(70.51, 285.8) * mm});
            skLineSegment(sketch, "E437", {"start": v(70.51, 285.8) * mm, "end": v(76.98, 285.8) * mm});
            skLineSegment(sketch, "E438", {"start": v(-76.98, 94.27) * mm, "end": v(-76.98, 101.67) * mm});
            skLineSegment(sketch, "E439", {"start": v(-76.98, 101.67) * mm, "end": v(-81.37, 101.67) * mm});
            skLineSegment(sketch, "E440", {"start": v(-76.98, 113.45) * mm, "end": v(-81.37, 113.45) * mm});
            skLineSegment(sketch, "E441", {"start": v(-76.98, 113.45) * mm, "end": v(-76.98, 125.23) * mm});
            skLineSegment(sketch, "E442", {"start": v(-76.98, 125.23) * mm, "end": v(-81.37, 125.23) * mm});
            skLineSegment(sketch, "E443", {"start": v(-81.37, 125.23) * mm, "end": v(-81.37, 137.01) * mm});
            skLineSegment(sketch, "E444", {"start": v(-76.98, 137.01) * mm, "end": v(-81.37, 137.01) * mm});
            skLineSegment(sketch, "E445", {"start": v(-76.98, 137.01) * mm, "end": v(-76.98, 148.8) * mm});
            skLineSegment(sketch, "E446", {"start": v(-76.98, 148.8) * mm, "end": v(-81.37, 148.8) * mm});
            skLineSegment(sketch, "E447", {"start": v(-81.37, 148.8) * mm, "end": v(-81.37, 160.58) * mm});
            skLineSegment(sketch, "E448", {"start": v(-76.98, 160.58) * mm, "end": v(-81.37, 160.58) * mm});
            skLineSegment(sketch, "E449", {"start": v(-76.98, 160.58) * mm, "end": v(-76.98, 172.36) * mm});
            skLineSegment(sketch, "E450", {"start": v(-76.98, 172.36) * mm, "end": v(-81.37, 172.36) * mm});
            skLineSegment(sketch, "E451", {"start": v(-81.37, 172.36) * mm, "end": v(-81.37, 184.14) * mm});
            skLineSegment(sketch, "E452", {"start": v(-76.98, 184.14) * mm, "end": v(-81.37, 184.14) * mm});
            skLineSegment(sketch, "E453", {"start": v(-76.98, 184.14) * mm, "end": v(-76.98, 195.92) * mm});
            skLineSegment(sketch, "E454", {"start": v(-76.98, 195.92) * mm, "end": v(-81.37, 195.92) * mm});
            skLineSegment(sketch, "E455", {"start": v(-81.37, 195.92) * mm, "end": v(-81.37, 207.7) * mm});
            skLineSegment(sketch, "E456", {"start": v(-76.98, 207.7) * mm, "end": v(-81.37, 207.7) * mm});
            skLineSegment(sketch, "E457", {"start": v(-76.98, 207.7) * mm, "end": v(-76.98, 219.48) * mm});
            skLineSegment(sketch, "E458", {"start": v(-76.98, 219.48) * mm, "end": v(-81.37, 219.48) * mm});
            skLineSegment(sketch, "E459", {"start": v(-81.37, 219.48) * mm, "end": v(-81.37, 231.26) * mm});
            skLineSegment(sketch, "E460", {"start": v(-76.98, 231.26) * mm, "end": v(-81.37, 231.26) * mm});
            skLineSegment(sketch, "E461", {"start": v(-76.98, 231.26) * mm, "end": v(-76.98, 243.05) * mm});
            skLineSegment(sketch, "E462", {"start": v(-76.98, 243.05) * mm, "end": v(-81.37, 243.05) * mm});
            skLineSegment(sketch, "E463", {"start": v(-81.37, 243.05) * mm, "end": v(-81.37, 254.83) * mm});
            skLineSegment(sketch, "E464", {"start": v(-76.98, 254.83) * mm, "end": v(-81.37, 254.83) * mm});
            skLineSegment(sketch, "E465", {"start": v(-76.98, 254.83) * mm, "end": v(-76.98, 266.6) * mm});
            skLineSegment(sketch, "E466", {"start": v(-76.98, 266.6) * mm, "end": v(-81.37, 266.6) * mm});
            skLineSegment(sketch, "E467", {"start": v(-76.98, 278.39) * mm, "end": v(-81.37, 278.39) * mm});
            skLineSegment(sketch, "E468", {"start": v(-76.98, 278.39) * mm, "end": v(-76.98, 285.8) * mm});
            skLineSegment(sketch, "E469", {"start": v(76.98, 94.27) * mm, "end": v(76.98, 101.67) * mm});
            skLineSegment(sketch, "E470", {"start": v(81.36, 101.67) * mm, "end": v(76.98, 101.67) * mm});
            skLineSegment(sketch, "E471", {"start": v(81.36, 113.45) * mm, "end": v(76.98, 113.45) * mm});
            skLineSegment(sketch, "E472", {"start": v(76.98, 113.45) * mm, "end": v(76.98, 125.23) * mm});
            skLineSegment(sketch, "E473", {"start": v(81.36, 125.23) * mm, "end": v(76.98, 125.23) * mm});
            skLineSegment(sketch, "E474", {"start": v(81.36, 125.23) * mm, "end": v(81.36, 137.01) * mm});
            skLineSegment(sketch, "E475", {"start": v(81.36, 137.01) * mm, "end": v(76.98, 137.01) * mm});
            skLineSegment(sketch, "E476", {"start": v(76.98, 137.01) * mm, "end": v(76.98, 148.8) * mm});
            skLineSegment(sketch, "E477", {"start": v(81.36, 148.8) * mm, "end": v(76.98, 148.8) * mm});
            skLineSegment(sketch, "E478", {"start": v(81.36, 148.8) * mm, "end": v(81.36, 160.58) * mm});
            skLineSegment(sketch, "E479", {"start": v(81.36, 160.58) * mm, "end": v(76.98, 160.58) * mm});
            skLineSegment(sketch, "E480", {"start": v(76.98, 160.58) * mm, "end": v(76.98, 172.36) * mm});
            skLineSegment(sketch, "E481", {"start": v(81.36, 172.36) * mm, "end": v(76.98, 172.36) * mm});
            skLineSegment(sketch, "E482", {"start": v(81.36, 172.36) * mm, "end": v(81.36, 184.14) * mm});
            skLineSegment(sketch, "E483", {"start": v(81.36, 184.14) * mm, "end": v(76.98, 184.14) * mm});
            skLineSegment(sketch, "E484", {"start": v(76.98, 184.14) * mm, "end": v(76.98, 195.92) * mm});
            skLineSegment(sketch, "E485", {"start": v(81.36, 195.92) * mm, "end": v(76.98, 195.92) * mm});
            skLineSegment(sketch, "E486", {"start": v(81.36, 195.92) * mm, "end": v(81.36, 207.7) * mm});
            skLineSegment(sketch, "E487", {"start": v(81.36, 207.7) * mm, "end": v(76.98, 207.7) * mm});
            skLineSegment(sketch, "E488", {"start": v(76.98, 207.7) * mm, "end": v(76.98, 219.48) * mm});
            skLineSegment(sketch, "E489", {"start": v(81.36, 219.48) * mm, "end": v(76.98, 219.48) * mm});
            skLineSegment(sketch, "E490", {"start": v(81.36, 219.48) * mm, "end": v(81.36, 231.26) * mm});
            skLineSegment(sketch, "E491", {"start": v(81.36, 231.26) * mm, "end": v(76.98, 231.26) * mm});
            skLineSegment(sketch, "E492", {"start": v(76.98, 231.26) * mm, "end": v(76.98, 243.05) * mm});
            skLineSegment(sketch, "E493", {"start": v(81.36, 243.05) * mm, "end": v(76.98, 243.05) * mm});
            skLineSegment(sketch, "E494", {"start": v(81.36, 243.05) * mm, "end": v(81.36, 254.83) * mm});
            skLineSegment(sketch, "E495", {"start": v(81.36, 254.83) * mm, "end": v(76.98, 254.83) * mm});
            skLineSegment(sketch, "E496", {"start": v(76.98, 254.83) * mm, "end": v(76.98, 266.6) * mm});
            skLineSegment(sketch, "E497", {"start": v(81.36, 266.6) * mm, "end": v(76.98, 266.6) * mm});
            skLineSegment(sketch, "E498", {"start": v(81.36, 278.39) * mm, "end": v(76.98, 278.39) * mm});
            skLineSegment(sketch, "E499", {"start": v(76.98, 278.39) * mm, "end": v(76.98, 285.8) * mm});
            skLineSegment(sketch, "E500", {"start": v(-81.37, -16.71) * mm, "end": v(-94.07, -16.71) * mm});
            skLineSegment(sketch, "E501", {"start": v(-94.07, -16.71) * mm, "end": v(-94.07, -28.5) * mm});
            skLineSegment(sketch, "E502", {"start": v(-94.07, -28.5) * mm, "end": v(-81.37, -28.5) * mm});
            skLineSegment(sketch, "E503", {"start": v(81.36, -28.5) * mm, "end": v(94.06, -28.5) * mm});
            skLineSegment(sketch, "E504", {"start": v(94.06, -28.5) * mm, "end": v(94.06, -16.71) * mm});
            skLineSegment(sketch, "E505", {"start": v(94.06, -16.71) * mm, "end": v(81, -16.71) * mm});
            skLineSegment(sketch, "E506", {"start": v(-81.37, -181.65) * mm, "end": v(-90.34, -181.65) * mm});
            skLineSegment(sketch, "E507", {"start": v(-90.34, -181.65) * mm, "end": v(-90.34, -193.43) * mm});
            skLineSegment(sketch, "E508", {"start": v(-90.34, -193.43) * mm, "end": v(-77.64, -193.43) * mm});
            skPoint(sketch, "E509.endSnap0", {"position": v(79.17, -181.65) * mm});
            skLineSegment(sketch, "E510", {"start": v(81.36, -181.65) * mm, "end": v(94.06, -181.65) * mm});
            skLineSegment(sketch, "E511", {"start": v(94.06, -193.43) * mm, "end": v(85.75, -193.43) * mm});
            skLineSegment(sketch, "E512", {"start": v(76.98, -193.43) * mm, "end": v(81.36, -193.43) * mm});
            skLineSegment(sketch, "E513", {"start": v(81.36, 113.45) * mm, "end": v(94.06, 113.45) * mm});
            skLineSegment(sketch, "E514", {"start": v(94.06, 113.45) * mm, "end": v(94.06, 101.67) * mm});
            skLineSegment(sketch, "E515", {"start": v(94.06, 101.67) * mm, "end": v(81.36, 101.67) * mm});
            skLineSegment(sketch, "E516", {"start": v(81.36, 278.39) * mm, "end": v(94.06, 278.39) * mm});
            skLineSegment(sketch, "E517", {"start": v(94.06, 278.39) * mm, "end": v(94.06, 266.6) * mm});
            skLineSegment(sketch, "E518", {"start": v(94.06, 266.6) * mm, "end": v(81.36, 266.6) * mm});
            skLineSegment(sketch, "E519", {"start": v(0, 301.75) * mm, "end": v(0, 0) * mm, "construction": true});
            skLineSegment(sketch, "E520.MirrorCS", {"start": v(-81.36, 278.39) * mm, "end": v(-94.06, 278.39) * mm});
            skLineSegment(sketch, "E521.MirrorCS", {"start": v(-94.06, 278.39) * mm, "end": v(-94.06, 266.6) * mm});
            skLineSegment(sketch, "E522.MirrorCS", {"start": v(-94.06, 266.6) * mm, "end": v(-81.36, 266.6) * mm});
            skLineSegment(sketch, "E523.MirrorCS", {"start": v(-94.06, 113.45) * mm, "end": v(-94.06, 101.67) * mm});
            skLineSegment(sketch, "E524.MirrorCS", {"start": v(-94.06, 101.67) * mm, "end": v(-81.36, 101.67) * mm});
            skLineSegment(sketch, "E525.MirrorCS", {"start": v(-81.36, 113.45) * mm, "end": v(-94.06, 113.45) * mm});
            skLineSegment(sketch, "E526", {"start": v(190.51, -85.46) * mm, "end": v(202.3, -85.46) * mm});
            skLineSegment(sketch, "E527", {"start": v(202.3, -81.08) * mm, "end": v(202.3, -85.46) * mm});
            skLineSegment(sketch, "E528", {"start": v(202.3, -81.08) * mm, "end": v(214.07, -81.08) * mm});
            skLineSegment(sketch, "E529", {"start": v(214.07, -81.08) * mm, "end": v(214.07, -85.46) * mm});
            skLineSegment(sketch, "E530", {"start": v(214.07, -85.46) * mm, "end": v(225.86, -85.46) * mm});
            skLineSegment(sketch, "E531", {"start": v(225.86, -81.08) * mm, "end": v(225.86, -85.46) * mm});
            skLineSegment(sketch, "E532", {"start": v(225.86, -81.08) * mm, "end": v(237.64, -81.08) * mm});
            skLineSegment(sketch, "E533", {"start": v(237.64, -81.08) * mm, "end": v(237.64, -85.46) * mm});
            skLineSegment(sketch, "E534", {"start": v(237.64, -85.46) * mm, "end": v(249.42, -85.46) * mm});
            skLineSegment(sketch, "E535", {"start": v(249.42, -81.08) * mm, "end": v(249.42, -85.46) * mm});
            skLineSegment(sketch, "E536", {"start": v(249.42, -81.08) * mm, "end": v(261.2, -81.08) * mm});
            skLineSegment(sketch, "E537", {"start": v(261.2, -81.08) * mm, "end": v(261.2, -85.46) * mm});
            skLineSegment(sketch, "E538", {"start": v(261.2, -85.46) * mm, "end": v(272.98, -85.46) * mm});
            skLineSegment(sketch, "E539", {"start": v(272.98, -81.08) * mm, "end": v(272.98, -85.46) * mm});
            skLineSegment(sketch, "E540", {"start": v(272.98, -81.08) * mm, "end": v(284.76, -81.08) * mm});
            skLineSegment(sketch, "E541", {"start": v(284.76, -81.08) * mm, "end": v(284.76, -85.46) * mm});
            skLineSegment(sketch, "E542", {"start": v(284.76, -85.46) * mm, "end": v(296.54, -85.46) * mm});
            skLineSegment(sketch, "E543", {"start": v(296.54, -81.08) * mm, "end": v(296.54, -85.46) * mm});
            skLineSegment(sketch, "E544", {"start": v(296.54, -81.08) * mm, "end": v(308.32, -81.08) * mm});
            skLineSegment(sketch, "E545", {"start": v(308.32, -81.08) * mm, "end": v(308.32, -85.46) * mm});
            skLineSegment(sketch, "E546", {"start": v(308.32, -85.46) * mm, "end": v(320.1, -85.46) * mm});
            skLineSegment(sketch, "E547", {"start": v(320.1, -81.08) * mm, "end": v(320.1, -85.46) * mm});
            skLineSegment(sketch, "E548", {"start": v(320.1, -81.08) * mm, "end": v(331.89, -81.08) * mm});
            skLineSegment(sketch, "E549", {"start": v(331.89, -81.08) * mm, "end": v(331.89, -85.46) * mm});
            skLineSegment(sketch, "E550", {"start": v(331.89, -85.46) * mm, "end": v(343.67, -85.46) * mm});
            skLineSegment(sketch, "E551", {"start": v(343.67, -81.08) * mm, "end": v(343.67, -85.46) * mm});
            skLineSegment(sketch, "E552", {"start": v(343.67, -81.08) * mm, "end": v(355.45, -81.08) * mm});
            skLineSegment(sketch, "E553", {"start": v(355.45, -81.08) * mm, "end": v(355.45, -85.46) * mm});
            skLineSegment(sketch, "E554", {"start": v(355.45, -85.46) * mm, "end": v(367.23, -85.46) * mm});
            skLineSegment(sketch, "E555", {"start": v(367.23, -81.08) * mm, "end": v(367.23, -85.46) * mm});
            skLineSegment(sketch, "E556", {"start": v(367.23, -81.08) * mm, "end": v(379.01, -81.08) * mm});
            skLineSegment(sketch, "E557", {"start": v(379.01, -81.08) * mm, "end": v(379.01, -85.46) * mm});
            skLineSegment(sketch, "E558", {"start": v(379.01, -85.46) * mm, "end": v(386.41, -85.46) * mm});
            skLineSegment(sketch, "E559", {"start": v(190.51, -10.35) * mm, "end": v(202.3, -10.35) * mm});
            skLineSegment(sketch, "E560", {"start": v(202.3, -10.35) * mm, "end": v(202.3, -14.73) * mm});
            skLineSegment(sketch, "E561", {"start": v(202.3, -14.73) * mm, "end": v(214.07, -14.73) * mm});
            skLineSegment(sketch, "E562", {"start": v(214.07, -10.35) * mm, "end": v(214.07, -14.73) * mm});
            skLineSegment(sketch, "E563", {"start": v(214.07, -10.35) * mm, "end": v(225.86, -10.35) * mm});
            skLineSegment(sketch, "E564", {"start": v(225.86, -10.35) * mm, "end": v(225.86, -14.73) * mm});
            skLineSegment(sketch, "E565", {"start": v(225.86, -14.73) * mm, "end": v(237.64, -14.73) * mm});
            skLineSegment(sketch, "E566", {"start": v(237.64, -10.35) * mm, "end": v(237.64, -14.73) * mm});
            skLineSegment(sketch, "E567", {"start": v(237.64, -10.35) * mm, "end": v(249.42, -10.35) * mm});
            skLineSegment(sketch, "E568", {"start": v(249.42, -10.35) * mm, "end": v(249.42, -14.73) * mm});
            skLineSegment(sketch, "E569", {"start": v(249.42, -14.73) * mm, "end": v(261.2, -14.73) * mm});
            skLineSegment(sketch, "E570", {"start": v(261.2, -10.35) * mm, "end": v(261.2, -14.73) * mm});
            skLineSegment(sketch, "E571", {"start": v(261.2, -10.35) * mm, "end": v(272.98, -10.35) * mm});
            skLineSegment(sketch, "E572", {"start": v(272.98, -10.35) * mm, "end": v(272.98, -14.73) * mm});
            skLineSegment(sketch, "E573", {"start": v(272.98, -14.73) * mm, "end": v(284.76, -14.73) * mm});
            skLineSegment(sketch, "E574", {"start": v(284.76, -10.35) * mm, "end": v(284.76, -14.73) * mm});
            skLineSegment(sketch, "E575", {"start": v(284.76, -10.35) * mm, "end": v(296.54, -10.35) * mm});
            skLineSegment(sketch, "E576", {"start": v(296.54, -10.35) * mm, "end": v(296.54, -14.73) * mm});
            skLineSegment(sketch, "E577", {"start": v(296.54, -14.73) * mm, "end": v(308.32, -14.73) * mm});
            skLineSegment(sketch, "E578", {"start": v(308.32, -10.35) * mm, "end": v(308.32, -14.73) * mm});
            skLineSegment(sketch, "E579", {"start": v(308.32, -10.35) * mm, "end": v(320.1, -10.35) * mm});
            skLineSegment(sketch, "E580", {"start": v(320.1, -10.35) * mm, "end": v(320.1, -14.73) * mm});
            skLineSegment(sketch, "E581", {"start": v(320.1, -14.73) * mm, "end": v(331.89, -14.73) * mm});
            skLineSegment(sketch, "E582", {"start": v(331.89, -10.35) * mm, "end": v(331.89, -14.73) * mm});
            skLineSegment(sketch, "E583", {"start": v(331.89, -10.35) * mm, "end": v(343.67, -10.35) * mm});
            skLineSegment(sketch, "E584", {"start": v(343.67, -10.35) * mm, "end": v(343.67, -14.73) * mm});
            skLineSegment(sketch, "E585", {"start": v(343.67, -14.73) * mm, "end": v(355.45, -14.73) * mm});
            skLineSegment(sketch, "E586", {"start": v(355.45, -10.35) * mm, "end": v(355.45, -14.73) * mm});
            skLineSegment(sketch, "E587", {"start": v(355.45, -10.35) * mm, "end": v(367.23, -10.35) * mm});
            skLineSegment(sketch, "E588", {"start": v(367.23, -10.35) * mm, "end": v(367.23, -14.73) * mm});
            skLineSegment(sketch, "E589", {"start": v(367.23, -14.73) * mm, "end": v(379.01, -14.73) * mm});
            skLineSegment(sketch, "E590", {"start": v(379.01, -10.35) * mm, "end": v(379.01, -14.73) * mm});
            skLineSegment(sketch, "E591", {"start": v(379.01, -10.35) * mm, "end": v(386.41, -10.35) * mm});
            skLineSegment(sketch, "E592", {"start": v(190.51, -85.46) * mm, "end": v(190.51, -74.73) * mm});
            skLineSegment(sketch, "E593", {"start": v(194.9, -74.73) * mm, "end": v(190.51, -74.73) * mm});
            skLineSegment(sketch, "E594", {"start": v(194.9, -74.73) * mm, "end": v(194.9, -64) * mm});
            skLineSegment(sketch, "E595", {"start": v(194.9, -64) * mm, "end": v(190.51, -64) * mm});
            skLineSegment(sketch, "E596", {"start": v(190.51, -64) * mm, "end": v(190.51, -53.27) * mm});
            skLineSegment(sketch, "E597", {"start": v(194.9, -53.27) * mm, "end": v(190.51, -53.27) * mm});
            skLineSegment(sketch, "E598", {"start": v(194.9, -53.27) * mm, "end": v(194.9, -42.54) * mm});
            skLineSegment(sketch, "E599", {"start": v(194.9, -42.54) * mm, "end": v(190.51, -42.54) * mm});
            skLineSegment(sketch, "E600", {"start": v(190.51, -42.54) * mm, "end": v(190.51, -31.81) * mm});
            skLineSegment(sketch, "E601", {"start": v(194.9, -31.81) * mm, "end": v(190.51, -31.81) * mm});
            skLineSegment(sketch, "E602", {"start": v(194.9, -31.81) * mm, "end": v(194.9, -21.08) * mm});
            skLineSegment(sketch, "E603", {"start": v(194.9, -21.08) * mm, "end": v(190.51, -21.08) * mm});
            skLineSegment(sketch, "E604", {"start": v(190.51, -21.08) * mm, "end": v(190.51, -10.35) * mm});
            skLineSegment(sketch, "E605", {"start": v(386.41, -85.46) * mm, "end": v(386.41, -74.73) * mm});
            skLineSegment(sketch, "E606", {"start": v(390.8, -74.73) * mm, "end": v(386.41, -74.73) * mm});
            skLineSegment(sketch, "E607", {"start": v(390.8, -74.73) * mm, "end": v(390.8, -64) * mm});
            skLineSegment(sketch, "E608", {"start": v(390.8, -64) * mm, "end": v(386.41, -64) * mm});
            skLineSegment(sketch, "E609", {"start": v(386.41, -64) * mm, "end": v(386.41, -53.27) * mm});
            skLineSegment(sketch, "E610", {"start": v(390.8, -53.27) * mm, "end": v(386.41, -53.27) * mm});
            skLineSegment(sketch, "E611", {"start": v(390.8, -53.27) * mm, "end": v(390.8, -42.54) * mm});
            skLineSegment(sketch, "E612", {"start": v(390.8, -42.54) * mm, "end": v(386.41, -42.54) * mm});
            skLineSegment(sketch, "E613", {"start": v(386.41, -42.54) * mm, "end": v(386.41, -31.81) * mm});
            skLineSegment(sketch, "E614", {"start": v(390.8, -31.81) * mm, "end": v(386.41, -31.81) * mm});
            skLineSegment(sketch, "E615", {"start": v(390.8, -31.81) * mm, "end": v(390.8, -21.08) * mm});
            skLineSegment(sketch, "E616", {"start": v(390.8, -21.08) * mm, "end": v(386.41, -21.08) * mm});
            skLineSegment(sketch, "E617", {"start": v(386.41, -21.08) * mm, "end": v(386.41, -10.35) * mm});
            skPoint(sketch, "E618.endSnap0", {"position": v(178.46, -61.9) * mm});
            skPoint(sketch, "E619.endSnap0", {"position": v(194.9, -69.36) * mm});
            skLineSegment(sketch, "E620", {"start": v(94.06, -181.65) * mm, "end": v(94.06, -193.43) * mm});
            skSolve(sketch);
        }
        {
            var Q0;
            Q0 = qSketchRegion(id + "F0", true);
            extrude(context, id + "F1", {"entities" : qUnion([Q0]), "depth" : 25.4 * mm});
        }
    });
